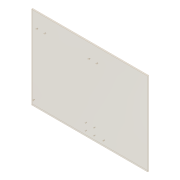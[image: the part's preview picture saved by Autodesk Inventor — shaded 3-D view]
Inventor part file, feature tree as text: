
AUTODESK INVENTOR PART (.ipt)
format: ipt  version: 2012 (Build 160160000, 160)  size: 99,328 bytes
history: native  units: in
note: dims shown in document units (in); Inventor stores cm internally (conversion verified against a paired STEP export)
features: hole x5, pattern_linear x3, extrude x1, sketch x1
ambient origin geometry x8: Origin, YZ Plane, XZ Plane, XY Plane, X Axis, Y Axis, Z Axis, Center Point
bodies: Solid1 (feature_tree)
feature tree (10):
  extrude  "Extrusion1"  Depth=31.5in
  hole  "Hole1"  [1 undecoded]
  pattern_linear  "Rectangular Pattern1"  Count1=2 Spacing1=2.625in
  hole  "Hole2"  [1 undecoded]
  pattern_linear  "Rectangular Pattern2"  Count1=2 Spacing1=3.0in
  hole  "Hole3"  [1 undecoded]
  pattern_linear  "Rectangular Pattern3"  [2 undecoded]
  hole  "Hole4"  [1 undecoded]
  hole  "Hole5"  [1 undecoded]
  sketch  "Sketch1"  dims[d0=44.0in d1=31.5in d2=0.5in d3=0.0in d4=20.4063in d5=1.625in d6=0.265in d7=0.75in d8=0.375in d9=0.25in d10=0.5635in d11=1.0in d12=0.8108in d13=0.7874in d15=2.625in d16=0.7874in d18=3.1875in d19=1.875in d20=5.625in d21=0.265in d22=0.75in d23=0.5in d24=0.25in d25=0.5635in d26=1.0in d27=0.8108in d28=0.7874in d30=3.0in d31=19.375in d32=5.625in d33=0.265in d34=0.75in d35=0.5in d36=0.25in d37=0.5635in d38=1.0in d39=0.8108in d40=0.7874in d42=3.0in d43=1.875in d44=0.625in d45=0.265in d46=0.75in d47=0.5in d48=0.25in d49=0.5635in d50=1.0in d51=0.8108in d52=16.75in d53=1.875in d54=0.265in d55=0.75in d56=0.5in d57=0.25in d58=0.5635in d59=1.0in d60=0.8108in]
note: 7 required parameter values undecoded (feature->parameter linkage not recoverable at this tier; creation-order binding heuristic only, values carry confidence <= 0.55)
